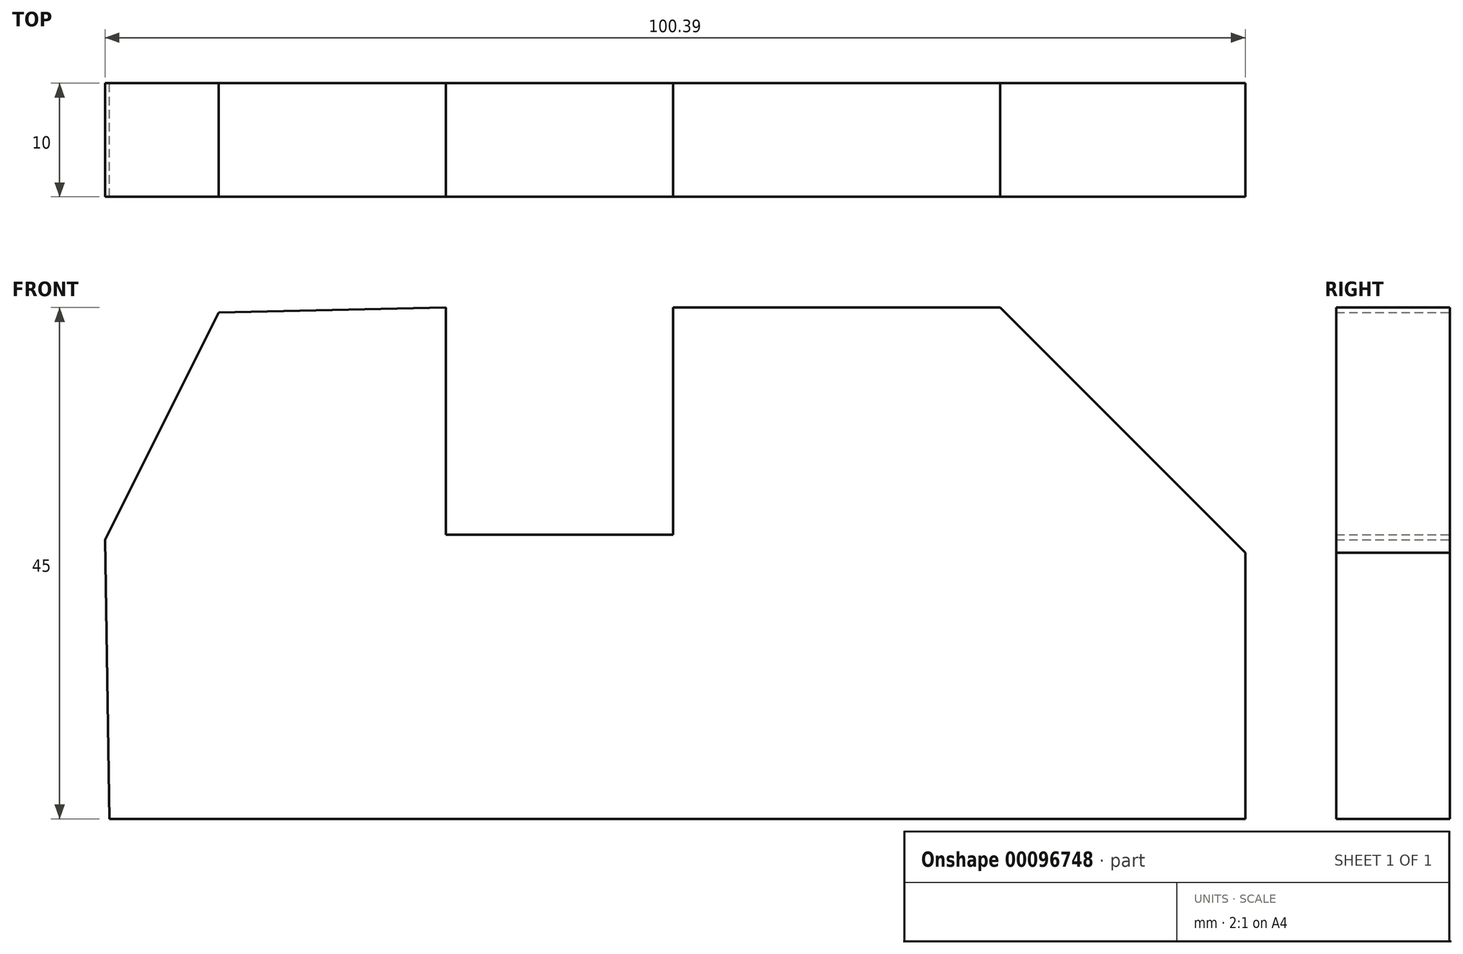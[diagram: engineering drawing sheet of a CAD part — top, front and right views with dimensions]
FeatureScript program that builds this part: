
annotation { "Feature Type Name" : "Feature", "Feature Type Description" : "" }
export const myFeature = defineFeature(function(context is Context, id is Id, definition is map)
    precondition{}
    {
        {
            var Q0;
            Q0=qCreatedBy(makeId("Front.planeOp"),FACE);
            var sketch = newSketch(context, id + "F0", { "sketchPlane" : qUnion([Q0])});
            skLineSegment(sketch, "E0", {"start": v(3.26, 0) * mm, "end": v(103.26, 0) * mm});
            skLineSegment(sketch, "E1", {"start": v(81.68, 45) * mm, "end": v(52.87, 45) * mm});
            skLineSegment(sketch, "E2", {"start": v(52.87, 45) * mm, "end": v(52.87, 25) * mm});
            skLineSegment(sketch, "E3", {"start": v(52.87, 25) * mm, "end": v(32.87, 25) * mm});
            skLineSegment(sketch, "E4", {"start": v(32.87, 25) * mm, "end": v(32.87, 45) * mm});
            skLineSegment(sketch, "E5", {"start": v(103.26, 0) * mm, "end": v(103.26, 23.42) * mm});
            skLineSegment(sketch, "E6", {"start": v(103.26, 23.42) * mm, "end": v(81.68, 45) * mm});
            skLineSegment(sketch, "E7", {"start": v(2.87, 24.57) * mm, "end": v(12.87, 44.57) * mm});
            skLineSegment(sketch, "E8", {"start": v(12.87, 44.57) * mm, "end": v(32.87, 45) * mm});
            skLineSegment(sketch, "E9", {"start": v(2.87, 24.57) * mm, "end": v(3.26, 0) * mm});
            skSolve(sketch);
        }
        {
            var Q0;
            Q0 = qSketchRegion(id + "F0", true);
            extrude(context, id + "F1", {"entities" : qUnion([Q0]), "depth" : 10 * mm});
        }
    });
